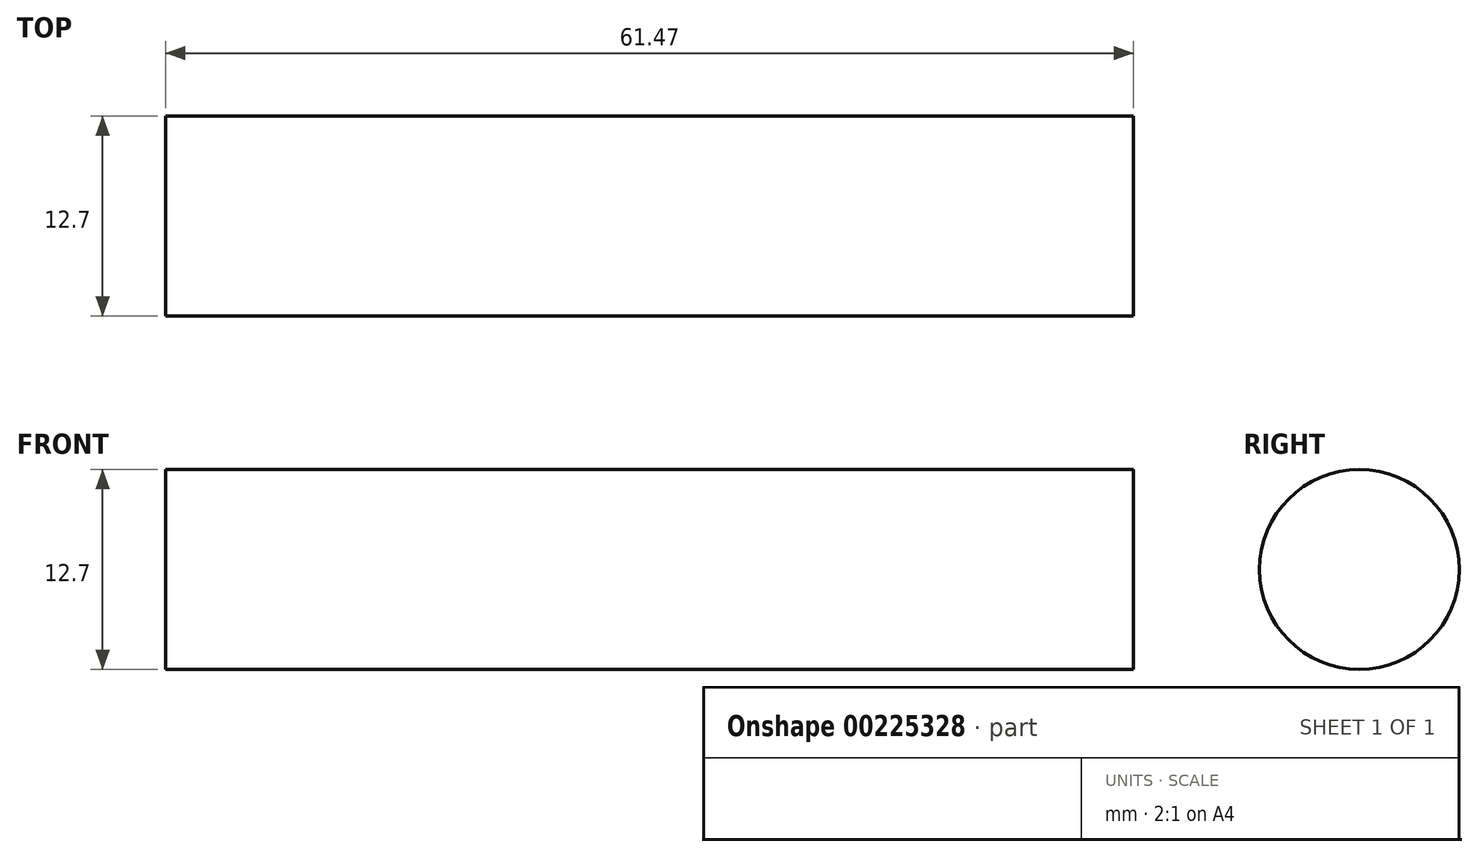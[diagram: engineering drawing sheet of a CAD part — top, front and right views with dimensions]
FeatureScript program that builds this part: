
annotation { "Feature Type Name" : "Feature", "Feature Type Description" : "" }
export const myFeature = defineFeature(function(context is Context, id is Id, definition is map)
    precondition{}
    {
        {
            var Q0;
            Q0=qCreatedBy(makeId("Right.planeOp"),FACE);
            var sketch = newSketch(context, id + "F0", { "sketchPlane" : qUnion([Q0])});
            skCircle(sketch, "E0", {"center": v(0, 0) * mm, "radius": 6.35 * mm});
            skSolve(sketch);
        }
        {
            var Q0;
            Q0 = qSketchRegion(id + "F0", true);
            extrude(context, id + "F1", {"entities" : qUnion([Q0]), "depth" : 61.47 * mm});
        }
    });
